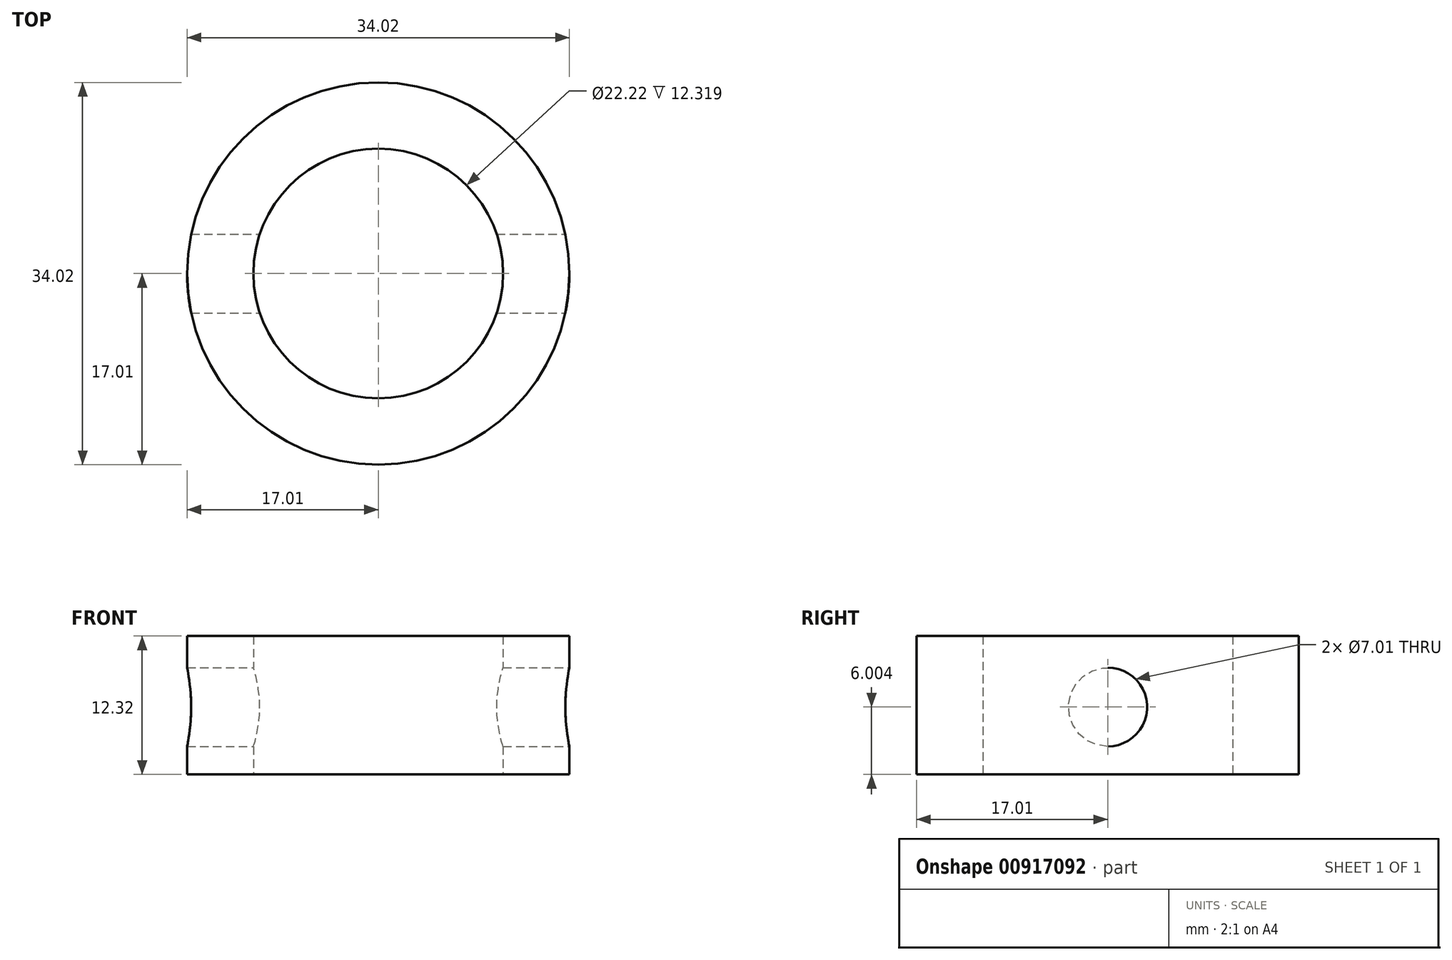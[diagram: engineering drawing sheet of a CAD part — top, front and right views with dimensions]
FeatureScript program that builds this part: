
annotation { "Feature Type Name" : "Feature", "Feature Type Description" : "" }
export const myFeature = defineFeature(function(context is Context, id is Id, definition is map)
    precondition{}
    {
        {
            var Q0;
            Q0=qCreatedBy(makeId("Top.planeOp"),FACE);
            var sketch = newSketch(context, id + "F0", { "sketchPlane" : qUnion([Q0])});
            skCircle(sketch, "E0", {"center": v(0, 0) * mm, "radius": 17 * mm});
            skSolve(sketch);
        }
        {
            var Q0;
            Q0 = qSketchRegion(id + "F0", true);
            extrude(context, id + "F1", {"entities" : qUnion([Q0]), "depth" : 12.32 * mm, "offsetDistance" : 25.4 * mm});
        }
        {
            var Q0;
            Q0=qCreatedBy(makeId("Right.planeOp"),FACE);
            var sketch = newSketch(context, id + "F2", { "sketchPlane" : qUnion([Q0])});
            skLineSegment(sketch, "E1", {"start": v(0, 0) * mm, "end": v(0, 2.5) * mm});
            skLineSegment(sketch, "E2", {"start": v(0, 2.5) * mm, "end": v(0, 9.5) * mm});
            skLineSegment(sketch, "E3", {"start": v(0, 9.5) * mm, "end": v(0, 6) * mm});
            skCircle(sketch, "E4", {"center": v(0, 6) * mm, "radius": 3.5 * mm});
            skSolve(sketch);
        }
        {
            var Q0;
            Q0 = qSketchRegion(id + "F2", true);
            extrude(context, id + "F3", {"entities" : qUnion([Q0]), "operationType" : NewBodyOperationType.REMOVE, "oppositeDirection" : true, "depth" : 25.4 * mm, "offsetDistance" : 25.4 * mm});
        }
        {
            var Q0;
            Q0=makeQuery(id+"F3.boolean.opBoolean","COPY",FACE,{"derivedFrom":makeQuery(id+"F3.opExtrude","CAP_FACE",FACE,{"disambiguationData":[OSD([sQuery(id+"F2.wireOp",EDGE,"E4")])],"isStart":true})});
            extrude(context, id + "F4", {"entities" : qUnion([Q0]), "operationType" : NewBodyOperationType.REMOVE, "oppositeDirection" : true, "depth" : 25.4 * mm, "offsetDistance" : 25.4 * mm});
        }
        {
            var Q0;
            Q0=makeQuery(id+"F1.opExtrude","CAP_FACE",FACE,{"disambiguationData":[OSD([sQuery(id+"F0.wireOp",EDGE,"E0")])],"isStart":true});
            var sketch = newSketch(context, id + "F5", { "sketchPlane" : qUnion([Q0])});
            skCircle(sketch, "E5", {"center": v(0, 0) * mm, "radius": 11.1 * mm});
            skSolve(sketch);
        }
        {
            var Q0;
            Q0 = qSketchRegion(id + "F5", true);
            extrude(context, id + "F6", {"entities" : qUnion([Q0]), "operationType" : NewBodyOperationType.REMOVE, "oppositeDirection" : true, "depth" : 25.4 * mm, "offsetDistance" : 25.4 * mm});
        }
    });
